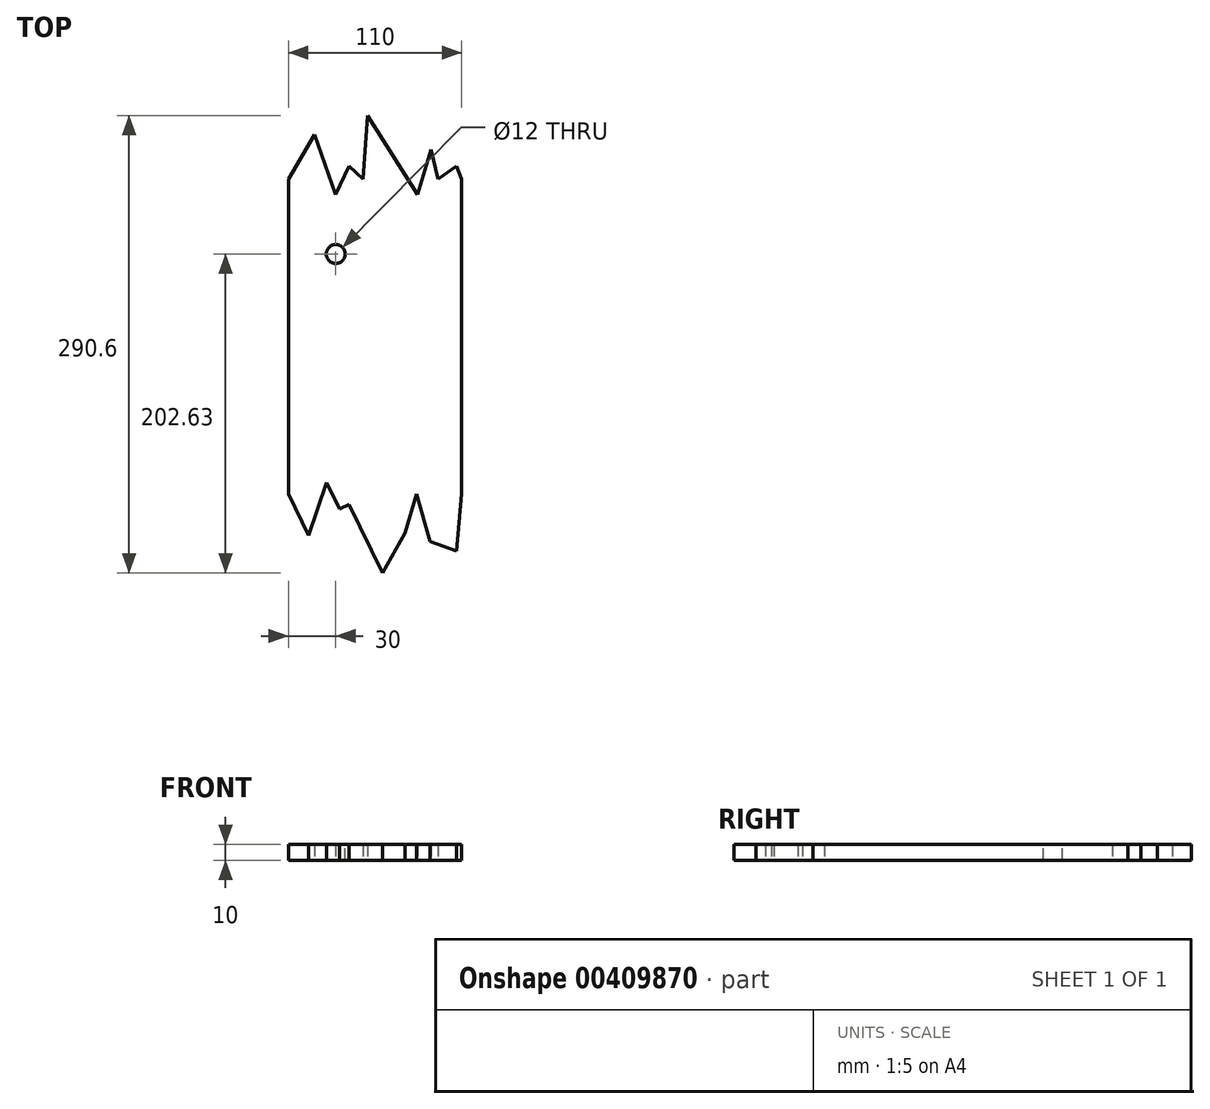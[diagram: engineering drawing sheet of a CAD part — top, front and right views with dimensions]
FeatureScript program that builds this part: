
annotation { "Feature Type Name" : "Feature", "Feature Type Description" : "" }
export const myFeature = defineFeature(function(context is Context, id is Id, definition is map)
    precondition{}
    {
        {
            var Q0;
            Q0=qCreatedBy(makeId("Top.planeOp"),FACE);
            var sketch = newSketch(context, id + "F0", { "sketchPlane" : qUnion([Q0])});
            skLineSegment(sketch, "E0.left", {"start": v(-55, -100) * mm, "end": v(-55, 100) * mm});
            skLineSegment(sketch, "E0.right", {"start": v(55, -100) * mm, "end": v(55, 100) * mm});
            skLineSegment(sketch, "E1", {"start": v(0, 100) * mm, "end": v(0, -100) * mm, "construction": true});
            skLineSegment(sketch, "E2", {"start": v(-55, 100) * mm, "end": v(-38.31, 128.38) * mm});
            skLineSegment(sketch, "E3", {"start": v(-38.31, 128.38) * mm, "end": v(-25.1, 90.2) * mm});
            skLineSegment(sketch, "E4", {"start": v(-25.1, 90.2) * mm, "end": v(-16.33, 108.43) * mm});
            skLineSegment(sketch, "E5", {"start": v(-16.33, 108.43) * mm, "end": v(-7.62, 100) * mm});
            skLineSegment(sketch, "E6", {"start": v(-7.62, 100) * mm, "end": v(-4.74, 140.47) * mm});
            skLineSegment(sketch, "E7", {"start": v(-4.74, 140.47) * mm, "end": v(26.93, 90.2) * mm});
            skLineSegment(sketch, "E8", {"start": v(26.93, 90.2) * mm, "end": v(35.73, 118.94) * mm});
            skLineSegment(sketch, "E9", {"start": v(35.73, 118.94) * mm, "end": v(40.09, 100) * mm});
            skLineSegment(sketch, "E10", {"start": v(40.09, 100) * mm, "end": v(51.68, 108.43) * mm});
            skLineSegment(sketch, "E11", {"start": v(51.68, 108.43) * mm, "end": v(55, 100) * mm});
            skLineSegment(sketch, "E12", {"start": v(-55, -100) * mm, "end": v(-42.33, -126.18) * mm});
            skLineSegment(sketch, "E13", {"start": v(-42.33, -126.18) * mm, "end": v(-30.67, -92.5) * mm});
            skLineSegment(sketch, "E14", {"start": v(-30.67, -92.5) * mm, "end": v(-22.48, -109.44) * mm});
            skLineSegment(sketch, "E15", {"start": v(-22.48, -109.44) * mm, "end": v(-16.33, -106.46) * mm});
            skLineSegment(sketch, "E16", {"start": v(-16.33, -106.46) * mm, "end": v(4.8, -150.13) * mm});
            skLineSegment(sketch, "E17", {"start": v(4.8, -150.13) * mm, "end": v(18.94, -124.54) * mm});
            skLineSegment(sketch, "E18", {"start": v(18.94, -124.54) * mm, "end": v(26.32, -100) * mm});
            skLineSegment(sketch, "E19", {"start": v(26.32, -100) * mm, "end": v(34.8, -130.02) * mm});
            skLineSegment(sketch, "E20", {"start": v(34.8, -130.02) * mm, "end": v(51.68, -136.18) * mm});
            skLineSegment(sketch, "E21", {"start": v(51.68, -136.18) * mm, "end": v(55, -100) * mm});
            skSolve(sketch);
        }
        {
            var Q0;
            Q0=qSketchRegion(id+"F0",true);
            extrude(context, id + "F1", {"entities" : qUnion([Q0]), "depth" : 10 * mm});
        }
        {
            var Q0;
            Q0=makeQuery(id+"F1.opExtrude","CAP_FACE",FACE,{"disambiguationData":[OSD([sQuery(id+"F0.wireOp",EDGE,"E0.bottom"),sQuery(id+"F0.wireOp",EDGE,"E0.top"),sQuery(id+"F0.wireOp",EDGE,"E0.left"),sQuery(id+"F0.wireOp",EDGE,"E0.right")])],"isStart":false});
            var sketch = newSketch(context, id + "F2", { "sketchPlane" : qUnion([Q0])});
            skCircle(sketch, "E22", {"center": v(-25, 52.5) * mm, "radius": 6 * mm});
            skPoint(sketch, "E23", {"position": v(0, 100) * mm});
            skLineSegment(sketch, "E24", {"start": v(0, 100) * mm, "end": v(0, -100) * mm, "construction": true});
            skLineSegment(sketch, "E25", {"start": v(-55, 0) * mm, "end": v(55, 0) * mm, "construction": true});
            skSolve(sketch);
        }
        {
            var Q0;
            Q0=qSketchRegion(id+"F2",true);
            extrude(context, id + "F3", {"entities" : qUnion([Q0]), "operationType" : NewBodyOperationType.REMOVE, "endBound" : BoundingType.THROUGH_ALL, "oppositeDirection" : true, "depth" : 25 * mm});
        }
    });
